# Revit family: Magnuson-HJW_Coat_Tree-11
name_source: partatom
category: Furniture
units: mm (PartAtom-declared; Revit-internal decimal feet)

## family parameters
Always vertical = Yes
Cut with Voids When Loaded = No
OmniClass Number = 23.40.20.00
OmniClass Title = General Furniture and Specialties
Room Calculation Point = No
Shared = No
Work Plane-Based = No

## types (1)
- HJW
    Assembly Code = E2020200
    Default Elevation = 0"
    Depth = 19 1/8"
    Description = Textured painted steel coat tree
    Height = 62 31/32"
    Keynote = 12500
    Low Emitting Finish = Yes
    Low Emitting Material = Yes
    Manufacturer = Magnuson Group
    Model = HJW
    Percentage of Recycled Content = 0
    Product Documentation Link = https://magnusongroup.com
    Revit Model Built By = https://servex-us.com
    Rod Finish = MAG - Textured painted steel
    Salvage or Reuse = Yes
    Type Comments = HJW
    URL = www.magnusongroup.com
    Width = 22 1/16"

## geometry (parser evidence)
native form markers: Sweep x2
no freeform markers — native parametric forms only
